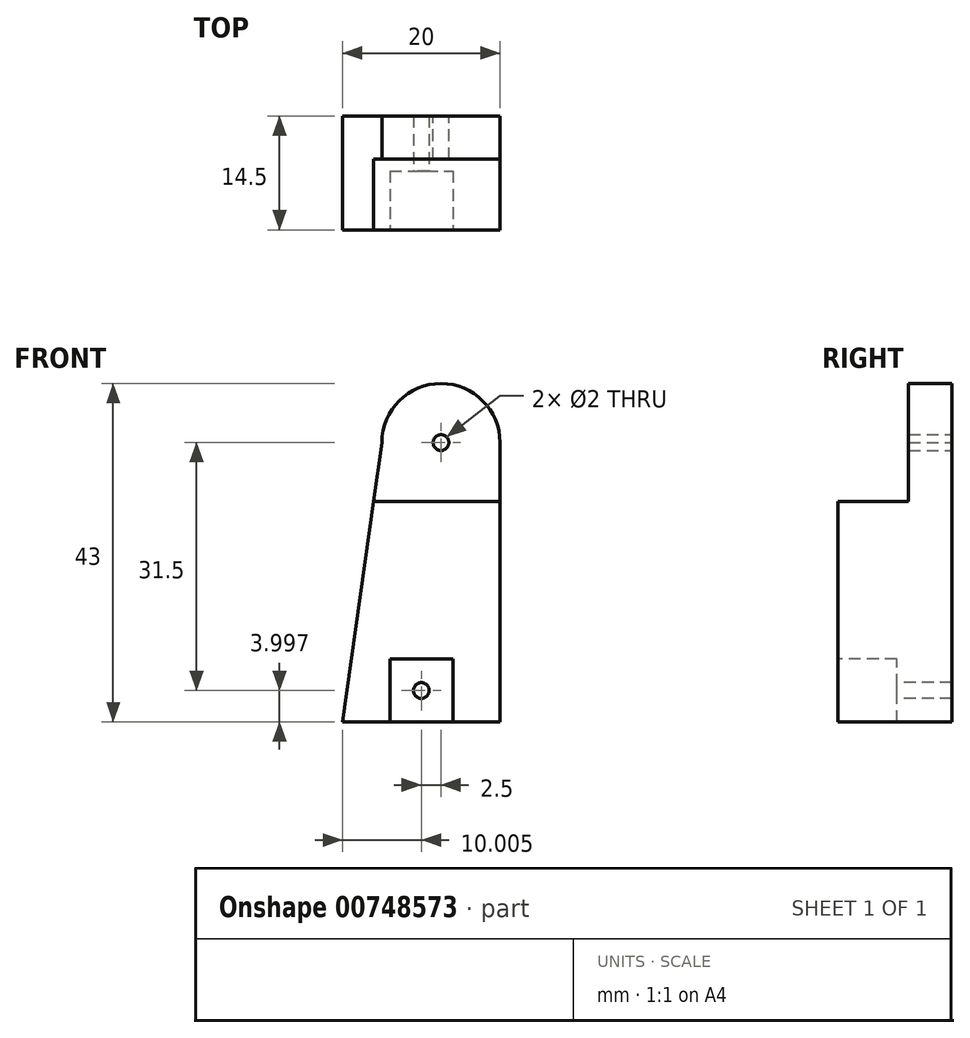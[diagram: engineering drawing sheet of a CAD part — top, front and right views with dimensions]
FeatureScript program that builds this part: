
annotation { "Feature Type Name" : "Feature", "Feature Type Description" : "" }
export const myFeature = defineFeature(function(context is Context, id is Id, definition is map)
    precondition{}
    {
        {
            var Q0;
            Q0=qCreatedBy(makeId("Front.planeOp"),FACE);
            var sketch = newSketch(context, id + "F0", { "sketchPlane" : qUnion([Q0])});
            skLineSegment(sketch, "E0.bottom", {"start": v(-52.7, 92.14) * mm, "end": v(-37.7, 92.14) * mm});
            skLineSegment(sketch, "E0.top", {"start": v(-52.7, -7.86) * mm, "end": v(-37.7, -7.86) * mm});
            skLineSegment(sketch, "E0.left", {"start": v(-52.7, 92.14) * mm, "end": v(-52.7, -7.86) * mm});
            skLineSegment(sketch, "E0.right", {"start": v(-37.7, 92.14) * mm, "end": v(-37.7, -7.86) * mm});
            skCircle(sketch, "E1", {"center": v(-45.2, 84.64) * mm, "radius": 1 * mm});
            skCircle(sketch, "E2", {"center": v(-45.2, 84.64) * mm, "radius": 7.5 * mm});
            skSolve(sketch);
        }
        {
            var Q0;
            Q0=makeQuery(id+"F0.imprint","IMPRINT",FACE,{"disambiguationData":[TD([[makeQuery(id+"F0.imprint","IMPRINT",EDGE,{"derivedFrom":sQuery(id+"F0.wireOp",EDGE,"E1")}),-1.0]])]});
            var Q1;
            {var subQ0=sQuery(id+"F0.wireOp",EDGE,"E0.top");Q1=makeQuery(id+"F0.imprint","IMPRINT",FACE,{"disambiguationData":[TD([[makeQuery(id+"F0.imprint","IMPRINT",EDGE,{"derivedFrom":subQ0}),1.0]])]});}
            extrude(context, id + "F1", {"entities" : qUnion([Q0, Q1]), "depth" : 5.5 * mm, "offsetDistance" : 25 * mm});
        }
        {
            var Q0;
            Q0=makeQuery(id+"F1.opExtrude","CAP_FACE",FACE,{"disambiguationData":[OSD([sQuery(id+"F0.wireOp",EDGE,"E0.top"),sQuery(id+"F0.wireOp",EDGE,"E0.left"),sQuery(id+"F0.wireOp",EDGE,"E0.right"),sQuery(id+"F0.wireOp",EDGE,"E1"),sQuery(id+"F0.wireOp",EDGE,"E2")])],"isStart":false});
            var sketch = newSketch(context, id + "F2", { "sketchPlane" : qUnion([Q0])});
            skLineSegment(sketch, "E3.bottom", {"start": v(-37.7, 77.14) * mm, "end": v(-52.7, 77.14) * mm});
            skLineSegment(sketch, "E3.top", {"start": v(-37.7, -7.86) * mm, "end": v(-52.7, -7.86) * mm});
            skLineSegment(sketch, "E3.left", {"start": v(-37.7, -7.86) * mm, "end": v(-37.7, 77.14) * mm});
            skLineSegment(sketch, "E3.right", {"start": v(-52.7, -7.86) * mm, "end": v(-52.7, 77.14) * mm});
            skCircle(sketch, "E4", {"center": v(-45.2, 84.64) * mm, "radius": 1.4 * mm});
            skSolve(sketch);
        }
        {
            var Q0;
            {var subQ0=sQuery(id+"F2.wireOp",EDGE,"E3.bottom");Q0=makeQuery(id+"F2.imprint","IMPRINT",FACE,{"disambiguationData":[TD([[makeQuery(id+"F2.imprint","IMPRINT",EDGE,{"derivedFrom":subQ0}),1.0]])]});}
            extrude(context, id + "F3", {"entities" : qUnion([Q0]), "operationType" : NewBodyOperationType.ADD, "depth" : 9 * mm, "offsetDistance" : 25 * mm});
        }
        {
            var Q0;
            Q0=makeQuery(id+"FcwPvkc5rE0Od8o_1.boolean.opBoolean","MERGE",FACE,{"derivedFrom":[makeQuery(id+"F3.boolean.opBoolean","MERGE",FACE,{"derivedFrom":[makeQuery(id+"F1.opExtrude","SWEPT_FACE",FACE,{"disambiguationData":[OSD([sQuery(id+"F0.wireOp",EDGE,"E0.right")])]}),makeQuery(id+"F3.opExtrude","SWEPT_FACE",FACE,{"disambiguationData":[OSD([sQuery(id+"F2.wireOp",EDGE,"E3.left")])]})]}),makeQuery(id+"FcwPvkc5rE0Od8o_1.opExtrude","CAP_FACE",FACE,{"disambiguationData":[OSD([sQuery(id+"F1XAVZx0FHQ3mT6_1.wireOp",EDGE,"SA4O7vyN-kzxW-E6y4-DIng-97i7dZC1EeCs.bottom"),sQuery(id+"F1XAVZx0FHQ3mT6_1.wireOp",EDGE,"SA4O7vyN-kzxW-E6y4-DIng-97i7dZC1EeCs.top"),sQuery(id+"F1XAVZx0FHQ3mT6_1.wireOp",EDGE,"SA4O7vyN-kzxW-E6y4-DIng-97i7dZC1EeCs.left"),sQuery(id+"F1XAVZx0FHQ3mT6_1.wireOp",EDGE,"pLlwk8R2-0Krg-EkIx-3mnF-K90o3AFMKjtp.left")])],"isStart":true})]});
            var sketch = newSketch(context, id + "F4", { "sketchPlane" : qUnion([Q0])});
            skLineSegment(sketch, "E5.bottom", {"start": v(-14.5, 77.14) * mm, "end": v(0, 77.14) * mm});
            skLineSegment(sketch, "E5.top", {"start": v(-14.5, 49.14) * mm, "end": v(0, 49.14) * mm});
            skLineSegment(sketch, "E5.left", {"start": v(-14.5, 77.14) * mm, "end": v(-14.5, 49.14) * mm});
            skLineSegment(sketch, "E5.right", {"start": v(0, 77.14) * mm, "end": v(0, 49.14) * mm});
            skSolve(sketch);
        }
        {
            var Q0;
            {var subQ0=sQuery(id+"F4.wireOp",EDGE,"E5.top");Q0=makeQuery(id+"F4.imprint","IMPRINT",FACE,{"disambiguationData":[TD([[makeQuery(id+"F4.imprint","IMPRINT",EDGE,{"derivedFrom":subQ0}),-1.0]])]});}
            extrude(context, id + "F5", {"entities" : qUnion([Q0]), "operationType" : NewBodyOperationType.REMOVE, "oppositeDirection" : true, "depth" : 25 * mm, "offsetDistance" : 25 * mm});
        }
        {
            var Q0;
            Q0=makeQuery(id+"F3.boolean.opBoolean","MERGE",FACE,{"derivedFrom":[makeQuery(id+"F1.opExtrude","SWEPT_FACE",FACE,{"disambiguationData":[OSD([sQuery(id+"F0.wireOp",EDGE,"E0.left")])]}),makeQuery(id+"F3.opExtrude","SWEPT_FACE",FACE,{"disambiguationData":[OSD([sQuery(id+"F2.wireOp",EDGE,"E3.right")])]})]});
            extrude(context, id + "F6", {"entities" : qUnion([Q0]), "operationType" : NewBodyOperationType.ADD, "depth" : 5 * mm, "offsetDistance" : 25 * mm});
        }
        {
            var Q0;
            {var subQ0=sQuery(id+"F0.wireOp",EDGE,"E0.left");Q0=makeQuery(id+"F6.boolean.opBoolean","MERGE",FACE,{"derivedFrom":[makeQuery(id+"FcwPvkc5rE0Od8o_1.boolean.opBoolean","MERGE",FACE,{"derivedFrom":[makeQuery(id+"F1.opExtrude","CAP_FACE",FACE,{"disambiguationData":[OSD([sQuery(id+"F0.wireOp",EDGE,"E0.top"),subQ0,sQuery(id+"F0.wireOp",EDGE,"E0.right"),sQuery(id+"F0.wireOp",EDGE,"E1"),sQuery(id+"F0.wireOp",EDGE,"E2")])],"isStart":true}),makeQuery(id+"FcwPvkc5rE0Od8o_1.opExtrude","SWEPT_FACE",FACE,{"disambiguationData":[OSD([sQuery(id+"F1XAVZx0FHQ3mT6_1.wireOp",EDGE,"SA4O7vyN-kzxW-E6y4-DIng-97i7dZC1EeCs.left")])]})]}),makeQuery(id+"F6.opExtrude","SWEPT_FACE",FACE,{"disambiguationData":[OSD([subQ0]),TDD([makeQuery(id+"F1.opExtrude","CAP_EDGE",EDGE,{"disambiguationData":[OSD([subQ0])],"isStart":true})])]})]});}
            var sketch = newSketch(context, id + "F7", { "sketchPlane" : qUnion([Q0])});
            skLineSegment(sketch, "E6", {"start": v(52.7, 84.64) * mm, "end": v(57.7, 49.14) * mm});
            skSolve(sketch);
        }
        {
            var Q0;
            Q0=makeQuery(id+"F7.imprint","IMPRINT",FACE,{"disambiguationData":[TD([[makeQuery(id+"F7.imprint","IMPRINT",EDGE,{"derivedFrom":sQuery(id+"F7.wireOp",EDGE,"E6")}),1.0]])]});
            extrude(context, id + "F8", {"entities" : qUnion([Q0]), "operationType" : NewBodyOperationType.REMOVE, "oppositeDirection" : true, "depth" : 25 * mm, "offsetDistance" : 25 * mm});
        }
        {
            var Q0;
            {var subQ0=sQuery(id+"F2.wireOp",EDGE,"E3.right");Q0=makeQuery(id+"F6.boolean.opBoolean","MERGE",FACE,{"derivedFrom":[makeQuery(id+"F3.opExtrude","CAP_FACE",FACE,{"disambiguationData":[OSD([sQuery(id+"F2.wireOp",EDGE,"E3.bottom"),sQuery(id+"F2.wireOp",EDGE,"E3.top"),sQuery(id+"F2.wireOp",EDGE,"E3.left"),subQ0])],"isStart":false}),makeQuery(id+"F6.opExtrude","SWEPT_FACE",FACE,{"disambiguationData":[OSD([subQ0])]})]});}
            var sketch = newSketch(context, id + "F9", { "sketchPlane" : qUnion([Q0])});
            skLineSegment(sketch, "E7.bottom", {"start": v(-51.7, 49.14) * mm, "end": v(-43.7, 49.14) * mm});
            skLineSegment(sketch, "E7.top", {"start": v(-51.7, 57.14) * mm, "end": v(-43.7, 57.14) * mm});
            skLineSegment(sketch, "E7.left", {"start": v(-51.7, 49.14) * mm, "end": v(-51.7, 57.14) * mm});
            skLineSegment(sketch, "E7.right", {"start": v(-43.7, 49.14) * mm, "end": v(-43.7, 57.14) * mm});
            skSolve(sketch);
        }
        {
            var Q0;
            Q0=makeQuery(id+"F9.imprint","IMPRINT",FACE,{"disambiguationData":[TD([[makeQuery(id+"F9.imprint","IMPRINT",EDGE,{"derivedFrom":sQuery(id+"F9.wireOp",EDGE,"E7.bottom")}),1.0]])]});
            extrude(context, id + "F10", {"entities" : qUnion([Q0]), "operationType" : NewBodyOperationType.REMOVE, "oppositeDirection" : true, "depth" : 7.5 * mm, "offsetDistance" : 25 * mm});
        }
        {
            var Q0;
            Q0=makeQuery(id+"F10.boolean.opBoolean","COPY",FACE,{"derivedFrom":makeQuery(id+"F10.opExtrude","CAP_FACE",FACE,{"disambiguationData":[OSD([sQuery(id+"F9.wireOp",EDGE,"E7.bottom"),sQuery(id+"F9.wireOp",EDGE,"E7.top"),sQuery(id+"F9.wireOp",EDGE,"E7.left"),sQuery(id+"F9.wireOp",EDGE,"E7.right")])],"isStart":false})});
            var sketch = newSketch(context, id + "F11", { "sketchPlane" : qUnion([Q0])});
            skCircle(sketch, "E8", {"center": v(-47.7, 53.14) * mm, "radius": 1 * mm});
            skPoint(sketch, "E8.centerSnap0", {"position": v(-43.7, 53.14) * mm});
            skPoint(sketch, "E8.centerSnap1", {"position": v(-47.7, 57.14) * mm});
            skSolve(sketch);
        }
        {
            var Q0;
            Q0=makeQuery(id+"F11.imprint","IMPRINT",FACE,{"disambiguationData":[TD([[makeQuery(id+"F11.imprint","IMPRINT",EDGE,{"derivedFrom":sQuery(id+"F11.wireOp",EDGE,"E8")}),1.0]])]});
            extrude(context, id + "F12", {"entities" : qUnion([Q0]), "operationType" : NewBodyOperationType.REMOVE, "oppositeDirection" : true, "depth" : 25 * mm, "offsetDistance" : 25 * mm});
        }
    });
